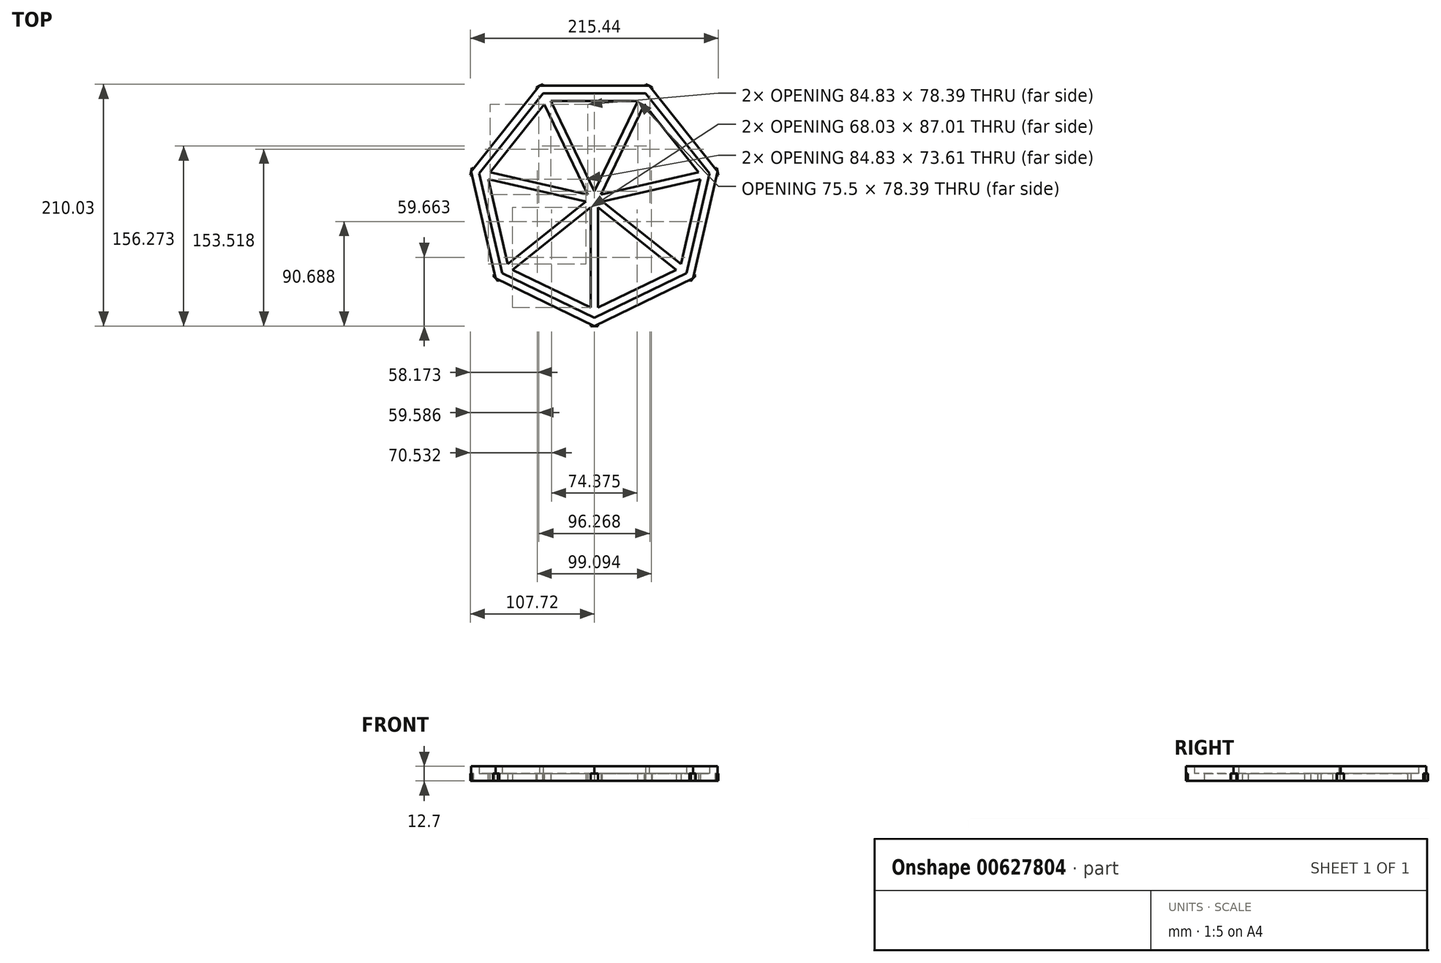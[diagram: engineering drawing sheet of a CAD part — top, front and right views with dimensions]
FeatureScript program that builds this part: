
annotation { "Feature Type Name" : "Feature", "Feature Type Description" : "" }
export const myFeature = defineFeature(function(context is Context, id is Id, definition is map)
    precondition{}
    {
        {
            var Q0;
            Q0=qCreatedBy(makeId("Top.planeOp"),FACE);
            var sketch = newSketch(context, id + "F0", { "sketchPlane" : qUnion([Q0])});
            skCircle(sketch, "E0.cCircle", {"center": v(0, 0) * mm, "radius": 98.9 * mm, "construction": true});
            skLineSegment(sketch, "E0.0", {"start": v(85.82, -68.44) * mm, "end": v(0, -109.76) * mm});
            skLineSegment(sketch, "E0.1", {"start": v(0, -109.76) * mm, "end": v(-85.82, -68.44) * mm});
            skLineSegment(sketch, "E0.2", {"start": v(-85.82, -68.44) * mm, "end": v(-107.01, 24.42) * mm});
            skLineSegment(sketch, "E0.3", {"start": v(-107.01, 24.42) * mm, "end": v(-47.63, 98.9) * mm});
            skLineSegment(sketch, "E0.4", {"start": v(-47.63, 98.9) * mm, "end": v(47.62, 98.9) * mm});
            skLineSegment(sketch, "E0.5", {"start": v(47.62, 98.9) * mm, "end": v(107.01, 24.42) * mm});
            skLineSegment(sketch, "E0.6", {"start": v(107.01, 24.42) * mm, "end": v(85.82, -68.44) * mm});
            skPoint(sketch, "E0.0.midPoint", {"position": v(42.9, -89.1) * mm});
            skCircle(sketch, "E1.cCircle", {"center": v(0, 0) * mm, "radius": 92.3 * mm, "construction": true});
            skLineSegment(sketch, "E1.0", {"start": v(80.1, -63.87) * mm, "end": v(0, -102.45) * mm});
            skLineSegment(sketch, "E1.1", {"start": v(0, -102.45) * mm, "end": v(-80.1, -63.87) * mm});
            skLineSegment(sketch, "E1.2", {"start": v(-80.1, -63.87) * mm, "end": v(-99.88, 22.8) * mm});
            skLineSegment(sketch, "E1.3", {"start": v(-99.88, 22.8) * mm, "end": v(-44.45, 92.3) * mm});
            skLineSegment(sketch, "E1.4", {"start": v(-44.45, 92.3) * mm, "end": v(44.45, 92.3) * mm});
            skLineSegment(sketch, "E1.5", {"start": v(44.45, 92.3) * mm, "end": v(99.88, 22.8) * mm});
            skLineSegment(sketch, "E1.6", {"start": v(99.88, 22.8) * mm, "end": v(80.1, -63.87) * mm});
            skPoint(sketch, "E1.0.midPoint", {"position": v(40.05, -83.16) * mm});
            skCircle(sketch, "E2.cCircle", {"center": v(0, 0) * mm, "radius": 85.7 * mm, "construction": true});
            skLineSegment(sketch, "E2.0", {"start": v(74.37, -59.31) * mm, "end": v(0, -95.13) * mm});
            skLineSegment(sketch, "E2.1", {"start": v(0, -95.13) * mm, "end": v(-74.37, -59.31) * mm});
            skLineSegment(sketch, "E2.2", {"start": v(-74.37, -59.31) * mm, "end": v(-92.74, 21.17) * mm});
            skLineSegment(sketch, "E2.3", {"start": v(-92.74, 21.17) * mm, "end": v(-41.27, 85.7) * mm});
            skLineSegment(sketch, "E2.4", {"start": v(-41.27, 85.7) * mm, "end": v(41.28, 85.7) * mm});
            skLineSegment(sketch, "E2.5", {"start": v(41.28, 85.7) * mm, "end": v(92.74, 21.17) * mm});
            skLineSegment(sketch, "E2.6", {"start": v(92.74, 21.17) * mm, "end": v(74.37, -59.31) * mm});
            skPoint(sketch, "E2.0.midPoint", {"position": v(37.19, -77.22) * mm});
            skLineSegment(sketch, "E3", {"start": v(-107.01, 24.42) * mm, "end": v(0, 0) * mm});
            skLineSegment(sketch, "E4", {"start": v(-47.63, 98.9) * mm, "end": v(0, 0) * mm});
            skLineSegment(sketch, "E5", {"start": v(47.63, 98.9) * mm, "end": v(0, 0) * mm});
            skLineSegment(sketch, "E6", {"start": v(107.01, 24.42) * mm, "end": v(0, 0) * mm});
            skLineSegment(sketch, "E7", {"start": v(85.82, -68.44) * mm, "end": v(0, 0) * mm});
            skLineSegment(sketch, "E8", {"start": v(0, -109.76) * mm, "end": v(0, 0) * mm});
            skLineSegment(sketch, "E9", {"start": v(-85.82, -68.44) * mm, "end": v(0, 0) * mm});
            skSolve(sketch);
        }
        {
            var Q0;
            Q0=sQuery(id+"F0.wireOp",EDGE,"E7");
            var Q1;
            Q1=sQuery(id+"F0.wireOp",EDGE,"E8");
            extrude(context, id + "F1", {"bodyType" : ToolBodyType.SURFACE, "surfaceEntities" : qUnion([Q0, Q1]), "depth" : 6.35 * mm, "offsetDistance" : 25.4 * mm});
        }
        {
            var Q0;
            Q0=makeQuery(id+"F1.opExtrude","SWEPT_FACE",FACE,{"disambiguationData":[OSD([sQuery(id+"F0.wireOp",EDGE,"E8")])]});
            extrude(context, id + "F2", {"entities" : qUnion([Q0]), "endBound" : BoundingType.SYMMETRIC, "depth" : 6.35 * mm, "offsetDistance" : 25.4 * mm});
        }
        {
            var Q0;
            Q0=makeQuery(id+"F1.opExtrude","SWEPT_FACE",FACE,{"disambiguationData":[OSD([sQuery(id+"F0.wireOp",EDGE,"E7")])]});
            extrude(context, id + "F3", {"entities" : qUnion([Q0]), "operationType" : NewBodyOperationType.ADD, "endBound" : BoundingType.SYMMETRIC, "depth" : 6.35 * mm, "offsetDistance" : 25.4 * mm});
        }
        {
            var Q0;
            Q0=sQuery(id+"F0.wireOp",EDGE,"E6");
            var Q1;
            Q1=sQuery(id+"F0.wireOp",EDGE,"E5");
            extrude(context, id + "F4", {"bodyType" : ToolBodyType.SURFACE, "surfaceEntities" : qUnion([Q0, Q1]), "depth" : 6.35 * mm, "offsetDistance" : 25.4 * mm});
        }
        {
            var Q0;
            Q0=makeQuery(id+"F4.opExtrude","SWEPT_FACE",FACE,{"disambiguationData":[OSD([sQuery(id+"F0.wireOp",EDGE,"E6")])]});
            extrude(context, id + "F5", {"entities" : qUnion([Q0]), "operationType" : NewBodyOperationType.ADD, "endBound" : BoundingType.SYMMETRIC, "depth" : 6.35 * mm, "offsetDistance" : 25.4 * mm});
        }
        {
            var Q0;
            Q0=makeQuery(id+"F4.opExtrude","SWEPT_FACE",FACE,{"disambiguationData":[OSD([sQuery(id+"F0.wireOp",EDGE,"E5")])]});
            extrude(context, id + "F6", {"entities" : qUnion([Q0]), "operationType" : NewBodyOperationType.ADD, "endBound" : BoundingType.SYMMETRIC, "depth" : 6.35 * mm, "offsetDistance" : 25.4 * mm});
        }
        {
            var Q0;
            Q0=sQuery(id+"F0.wireOp",EDGE,"E4");
            var Q1;
            Q1=sQuery(id+"F0.wireOp",EDGE,"E3");
            extrude(context, id + "F7", {"bodyType" : ToolBodyType.SURFACE, "surfaceEntities" : qUnion([Q0, Q1]), "depth" : 6.35 * mm, "offsetDistance" : 25.4 * mm});
        }
        {
            var Q0;
            Q0=makeQuery(id+"F7.opExtrude","SWEPT_FACE",FACE,{"disambiguationData":[OSD([sQuery(id+"F0.wireOp",EDGE,"E4")])]});
            extrude(context, id + "F8", {"entities" : qUnion([Q0]), "operationType" : NewBodyOperationType.ADD, "endBound" : BoundingType.SYMMETRIC, "depth" : 6.35 * mm, "offsetDistance" : 25.4 * mm});
        }
        {
            var Q0;
            Q0=makeQuery(id+"F7.opExtrude","SWEPT_FACE",FACE,{"disambiguationData":[OSD([sQuery(id+"F0.wireOp",EDGE,"E3")])]});
            extrude(context, id + "F9", {"entities" : qUnion([Q0]), "operationType" : NewBodyOperationType.ADD, "endBound" : BoundingType.SYMMETRIC, "depth" : 6.35 * mm, "offsetDistance" : 25.4 * mm});
        }
        {
            var Q0;
            Q0=sQuery(id+"F0.wireOp",EDGE,"E9");
            extrude(context, id + "F10", {"bodyType" : ToolBodyType.SURFACE, "surfaceEntities" : qUnion([Q0]), "depth" : 6.35 * mm, "offsetDistance" : 25.4 * mm});
        }
        {
            var Q0;
            Q0=makeQuery(id+"F10.opExtrude","SWEPT_FACE",FACE,{"disambiguationData":[OSD([sQuery(id+"F0.wireOp",EDGE,"E9")])]});
            extrude(context, id + "F11", {"entities" : qUnion([Q0]), "operationType" : NewBodyOperationType.ADD, "endBound" : BoundingType.SYMMETRIC, "depth" : 6.35 * mm, "offsetDistance" : 25.4 * mm});
        }
        {
            var Q0;
            {var subQ0=sQuery(id+"F0.wireOp",EDGE,"E0.4");Q0=makeQuery(id+"F0.imprint","IMPRINT",FACE,{"disambiguationData":[TD([[makeQuery(id+"F0.imprint","IMPRINT",EDGE,{"derivedFrom":subQ0}),-1.0]])]});}
            var Q1;
            {var subQ0=sQuery(id+"F0.wireOp",EDGE,"E0.5");Q1=makeQuery(id+"F0.imprint","IMPRINT",FACE,{"disambiguationData":[TD([[makeQuery(id+"F0.imprint","IMPRINT",EDGE,{"derivedFrom":subQ0}),-1.0]])]});}
            var Q2;
            {var subQ0=sQuery(id+"F0.wireOp",EDGE,"E0.6");Q2=makeQuery(id+"F0.imprint","IMPRINT",FACE,{"disambiguationData":[TD([[makeQuery(id+"F0.imprint","IMPRINT",EDGE,{"derivedFrom":subQ0}),-1.0]])]});}
            var Q3;
            {var subQ0=sQuery(id+"F0.wireOp",EDGE,"E0.0");Q3=makeQuery(id+"F0.imprint","IMPRINT",FACE,{"disambiguationData":[TD([[makeQuery(id+"F0.imprint","IMPRINT",EDGE,{"derivedFrom":subQ0}),-1.0]])]});}
            var Q4;
            {var subQ0=sQuery(id+"F0.wireOp",EDGE,"E0.1");Q4=makeQuery(id+"F0.imprint","IMPRINT",FACE,{"disambiguationData":[TD([[makeQuery(id+"F0.imprint","IMPRINT",EDGE,{"derivedFrom":subQ0}),-1.0]])]});}
            var Q5;
            {var subQ0=sQuery(id+"F0.wireOp",EDGE,"E0.2");Q5=makeQuery(id+"F0.imprint","IMPRINT",FACE,{"disambiguationData":[TD([[makeQuery(id+"F0.imprint","IMPRINT",EDGE,{"derivedFrom":subQ0}),-1.0]])]});}
            var Q6;
            {var subQ0=sQuery(id+"F0.wireOp",EDGE,"E0.3");Q6=makeQuery(id+"F0.imprint","IMPRINT",FACE,{"disambiguationData":[TD([[makeQuery(id+"F0.imprint","IMPRINT",EDGE,{"derivedFrom":subQ0}),-1.0]])]});}
            extrude(context, id + "F12", {"entities" : qUnion([Q0, Q1, Q2, Q3, Q4, Q5, Q6]), "operationType" : NewBodyOperationType.ADD, "depth" : 12.7 * mm, "offsetDistance" : 25.4 * mm});
        }
        {
            var Q0;
            {var subQ0=sQuery(id+"F0.wireOp",EDGE,"E1.5");Q0=makeQuery(id+"F0.imprint","IMPRINT",FACE,{"disambiguationData":[TD([[makeQuery(id+"F0.imprint","IMPRINT",EDGE,{"derivedFrom":subQ0}),-1.0]])]});}
            var Q1;
            {var subQ0=sQuery(id+"F0.wireOp",EDGE,"E1.4");Q1=makeQuery(id+"F0.imprint","IMPRINT",FACE,{"disambiguationData":[TD([[makeQuery(id+"F0.imprint","IMPRINT",EDGE,{"derivedFrom":subQ0}),-1.0]])]});}
            var Q2;
            {var subQ0=sQuery(id+"F0.wireOp",EDGE,"E1.3");Q2=makeQuery(id+"F0.imprint","IMPRINT",FACE,{"disambiguationData":[TD([[makeQuery(id+"F0.imprint","IMPRINT",EDGE,{"derivedFrom":subQ0}),-1.0]])]});}
            var Q3;
            {var subQ0=sQuery(id+"F0.wireOp",EDGE,"E1.2");Q3=makeQuery(id+"F0.imprint","IMPRINT",FACE,{"disambiguationData":[TD([[makeQuery(id+"F0.imprint","IMPRINT",EDGE,{"derivedFrom":subQ0}),-1.0]])]});}
            var Q4;
            {var subQ0=sQuery(id+"F0.wireOp",EDGE,"E1.1");Q4=makeQuery(id+"F0.imprint","IMPRINT",FACE,{"disambiguationData":[TD([[makeQuery(id+"F0.imprint","IMPRINT",EDGE,{"derivedFrom":subQ0}),-1.0]])]});}
            var Q5;
            {var subQ0=sQuery(id+"F0.wireOp",EDGE,"E1.0");Q5=makeQuery(id+"F0.imprint","IMPRINT",FACE,{"disambiguationData":[TD([[makeQuery(id+"F0.imprint","IMPRINT",EDGE,{"derivedFrom":subQ0}),-1.0]])]});}
            var Q6;
            {var subQ0=sQuery(id+"F0.wireOp",EDGE,"E1.6");Q6=makeQuery(id+"F0.imprint","IMPRINT",FACE,{"disambiguationData":[TD([[makeQuery(id+"F0.imprint","IMPRINT",EDGE,{"derivedFrom":subQ0}),-1.0]])]});}
            extrude(context, id + "F13", {"entities" : qUnion([Q0, Q1, Q2, Q3, Q4, Q5, Q6]), "operationType" : NewBodyOperationType.ADD, "depth" : 6.35 * mm, "offsetDistance" : 25.4 * mm});
        }
    });
